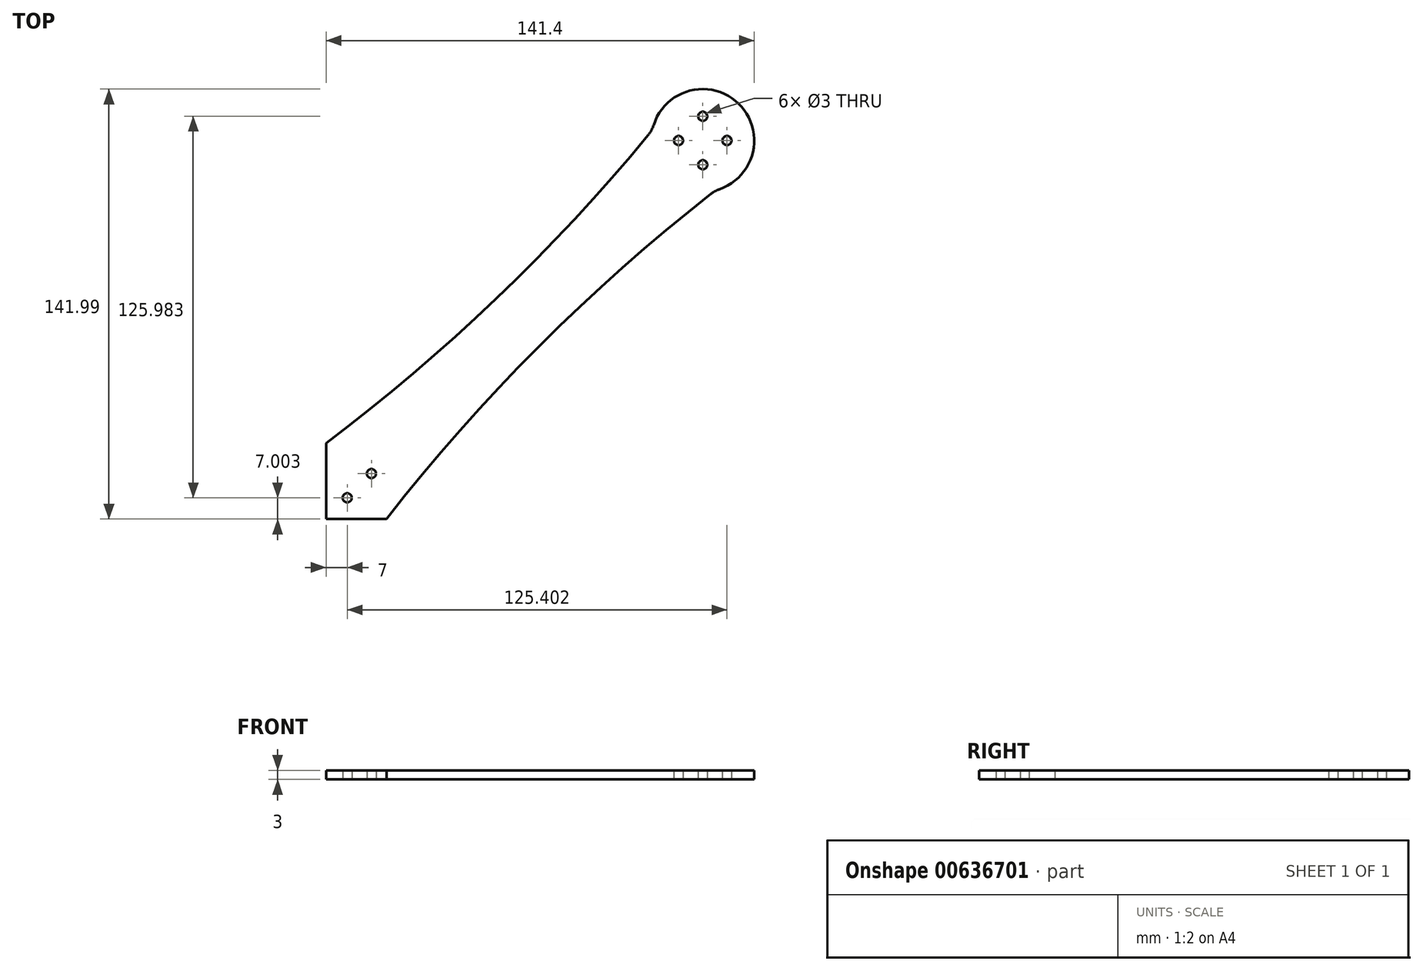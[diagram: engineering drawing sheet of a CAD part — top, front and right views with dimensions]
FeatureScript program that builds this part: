
annotation { "Feature Type Name" : "Feature", "Feature Type Description" : "" }
export const myFeature = defineFeature(function(context is Context, id is Id, definition is map)
    precondition{}
    {
        {
            var Q0;
            Q0=qCreatedBy(makeId("Top.planeOp"),FACE);
            var sketch = newSketch(context, id + "F0", { "sketchPlane" : qUnion([Q0])});
            skLineSegment(sketch, "E0", {"start": v(0, 0) * mm, "end": v(0, 25) * mm});
            skArc(sketch, "E1", {"start": v(129.98, 108.94) * mm, "mid": v(136.26, 137.18) * mm, "end": v(108.2, 130.13) * mm});
            skArc(sketch, "E2", {"start": v(0, 25) * mm, "mid": v(56.2, 72.75) * mm, "end": v(106.38, 126.79) * mm});
            skArc(sketch, "E3.MirrorCS", {"start": v(19.92, 0.01) * mm, "mid": v(70.24, 56.95) * mm, "end": v(127.1, 107.36) * mm});
            skLineSegment(sketch, "E4.MirrorCS", {"start": v(-0.08, 0.01) * mm, "end": v(19.92, 0.01) * mm});
            skPoint(sketch, "E5.visualSharp", {"position": v(107.76, 128.47) * mm});
            skArc(sketch, "E5.filletArc", {"start": v(106.38, 126.79) * mm, "mid": v(107.45, 128.37) * mm, "end": v(108.2, 130.13) * mm});
            skPoint(sketch, "E6.visualSharp", {"position": v(128.57, 108.51) * mm});
            skArc(sketch, "E6.filletArc", {"start": v(129.98, 108.94) * mm, "mid": v(128.48, 108.27) * mm, "end": v(127.1, 107.36) * mm});
            skCircle(sketch, "E7", {"center": v(124.4, 133) * mm, "radius": 1.5 * mm});
            skCircle(sketch, "E8", {"center": v(132.4, 125) * mm, "radius": 1.5 * mm});
            skCircle(sketch, "E9.MirrorC", {"center": v(116.4, 125) * mm, "radius": 1.5 * mm});
            skCircle(sketch, "E10.MirrorC", {"center": v(124.4, 117) * mm, "radius": 1.5 * mm});
            skCircle(sketch, "E11", {"center": v(7, 7.01) * mm, "radius": 1.5 * mm});
            skCircle(sketch, "E12", {"center": v(15, 15.01) * mm, "radius": 1.5 * mm});
            skSolve(sketch);
        }
        {
            var Q0;
            Q0=makeQuery(id+"F0.imprint","IMPRINT",FACE,{"disambiguationData":[TD([[makeQuery(id+"F0.imprint","IMPRINT",EDGE,{"derivedFrom":sQuery(id+"F0.wireOp",EDGE,"E1")}),1.0]])]});
            extrude(context, id + "F1", {"entities" : qUnion([Q0]), "depth" : 3 * mm, "offsetDistance" : 25 * mm});
        }
    });
